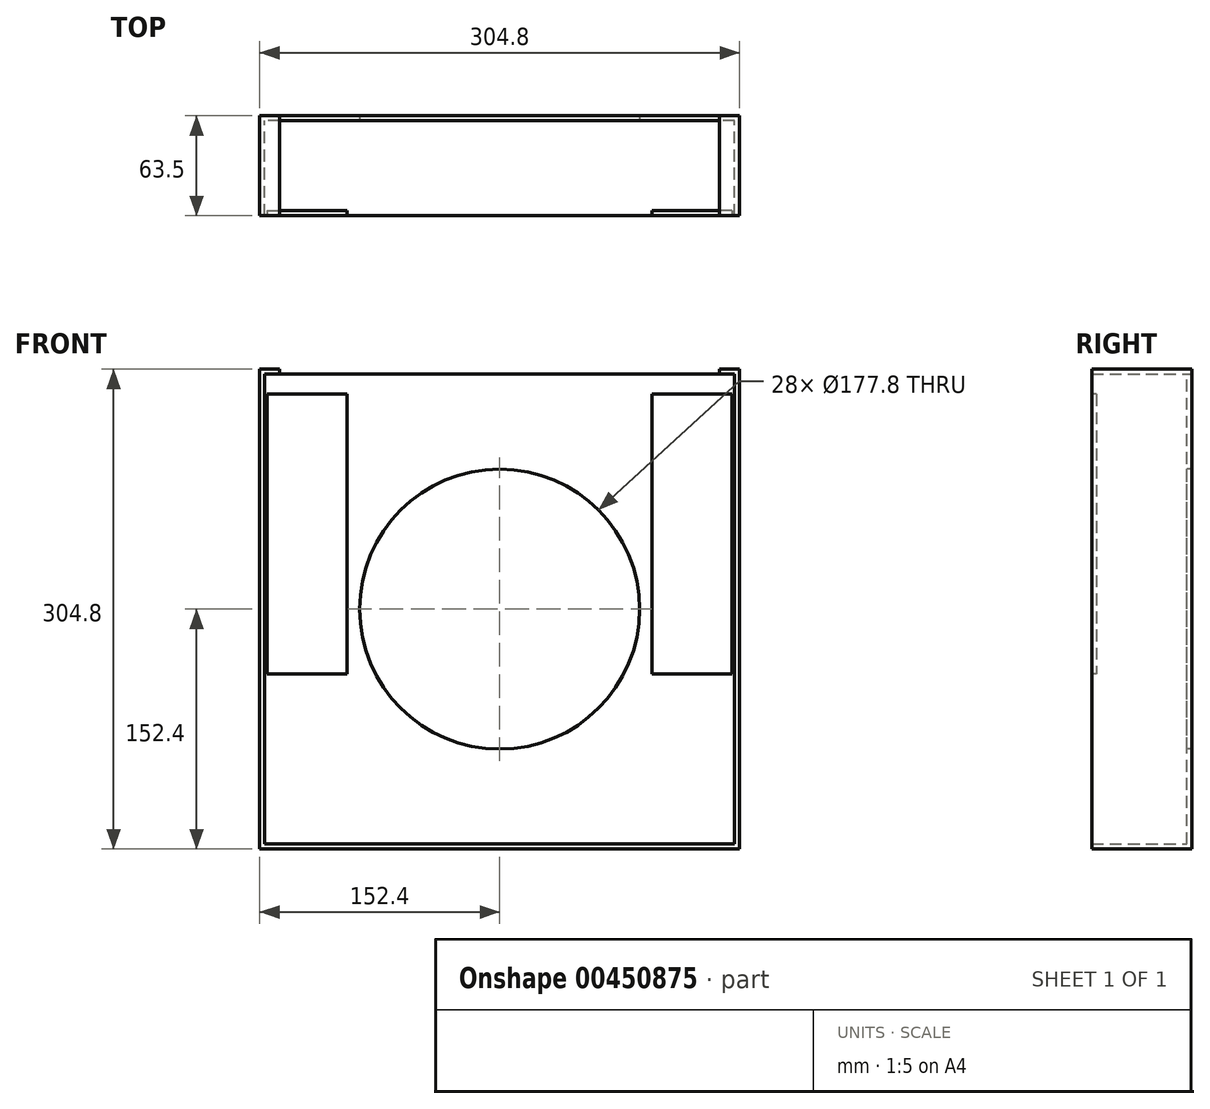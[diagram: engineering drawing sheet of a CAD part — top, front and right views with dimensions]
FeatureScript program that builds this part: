
annotation { "Feature Type Name" : "Feature", "Feature Type Description" : "" }
export const myFeature = defineFeature(function(context is Context, id is Id, definition is map)
    precondition{}
    {
        {
            var Q0;
            Q0=qCreatedBy(makeId("Front.planeOp"),FACE);
            var sketch = newSketch(context, id + "F0", { "sketchPlane" : qUnion([Q0])});
            skLineSegment(sketch, "E0.bottom", {"start": v(152.4, -152.4) * mm, "end": v(-152.4, -152.4) * mm});
            skLineSegment(sketch, "E0.top", {"start": v(152.4, 152.4) * mm, "end": v(-152.4, 152.4) * mm});
            skLineSegment(sketch, "E0.left", {"start": v(152.4, -152.4) * mm, "end": v(152.4, 152.4) * mm});
            skLineSegment(sketch, "E0.right", {"start": v(-152.4, -152.4) * mm, "end": v(-152.4, 152.4) * mm});
            skPoint(sketch, "E0.middle", {"position": v(0, 0) * mm});
            skSolve(sketch);
        }
        {
            var Q0;
            Q0=qSketchRegion(id+"F0",true);
            extrude(context, id + "F1", {"entities" : qUnion([Q0]), "depth" : 63.5 * mm});
        }
        {
            var Q0;
            Q0=makeQuery(id+"F1.opExtrude","CAP_FACE",FACE,{"disambiguationData":[OSD([sQuery(id+"F0.wireOp",EDGE,"E0.bottom"),sQuery(id+"F0.wireOp",EDGE,"E0.top"),sQuery(id+"F0.wireOp",EDGE,"E0.left"),sQuery(id+"F0.wireOp",EDGE,"E0.right")])],"isStart":false});
            shell(context, id + "F2", {"entities" : qUnion([Q0]), "thickness" : 3.17 * mm});
        }
        {
            var Q0;
            Q0=makeQuery(id+"F2.opShell","OFFSET_FACE",FACE,{"disambiguationData":[OSD([sQuery(id+"F0.wireOp",EDGE,"E0.bottom"),sQuery(id+"F0.wireOp",EDGE,"E0.top"),sQuery(id+"F0.wireOp",EDGE,"E0.left"),sQuery(id+"F0.wireOp",EDGE,"E0.right")])]});
            var sketch = newSketch(context, id + "F3", { "sketchPlane" : qUnion([Q0])});
            skCircle(sketch, "E1", {"center": v(0, 0) * mm, "radius": 88.9 * mm});
            skSolve(sketch);
        }
        {
            var Q0;
            Q0=qSketchRegion(id+"F3",true);
            extrude(context, id + "F4", {"entities" : qUnion([Q0]), "operationType" : NewBodyOperationType.REMOVE, "endBound" : BoundingType.UP_TO_NEXT, "oppositeDirection" : true, "depth" : 25.4 * mm});
        }
        {
            var Q0;
            Q0=makeQuery(id+"F1.opExtrude","CAP_FACE",FACE,{"disambiguationData":[OSD([sQuery(id+"F0.wireOp",EDGE,"E0.bottom"),sQuery(id+"F0.wireOp",EDGE,"E0.top"),sQuery(id+"F0.wireOp",EDGE,"E0.left"),sQuery(id+"F0.wireOp",EDGE,"E0.right")])],"isStart":false});
            var sketch = newSketch(context, id + "F5", { "sketchPlane" : qUnion([Q0])});
            skLineSegment(sketch, "E2.bottom", {"start": v(-147.64, 136.53) * mm, "end": v(-96.84, 136.53) * mm});
            skLineSegment(sketch, "E2.top", {"start": v(-147.64, -41.28) * mm, "end": v(-96.84, -41.28) * mm});
            skLineSegment(sketch, "E2.left", {"start": v(-147.64, 136.53) * mm, "end": v(-147.64, -41.28) * mm});
            skLineSegment(sketch, "E2.right", {"start": v(-96.84, 136.53) * mm, "end": v(-96.84, -41.28) * mm});
            skLineSegment(sketch, "E3.MirrorCS", {"start": v(147.64, 136.53) * mm, "end": v(96.84, 136.53) * mm});
            skLineSegment(sketch, "E4.MirrorCS", {"start": v(96.84, 136.53) * mm, "end": v(96.84, -41.28) * mm});
            skLineSegment(sketch, "E5.MirrorCS", {"start": v(147.64, -41.27) * mm, "end": v(96.84, -41.27) * mm});
            skLineSegment(sketch, "E6.MirrorCS", {"start": v(147.64, 136.53) * mm, "end": v(147.64, -41.28) * mm});
            skSolve(sketch);
        }
        {
            var Q0;
            Q0=makeQuery(id+"F5.imprint","IMPRINT",FACE,{"disambiguationData":[TD([[makeQuery(id+"F5.imprint","IMPRINT",EDGE,{"derivedFrom":sQuery(id+"F5.wireOp",EDGE,"E2.bottom")}),-1.0]])]});
            var Q1;
            Q1=makeQuery(id+"F5.imprint","IMPRINT",FACE,{"disambiguationData":[TD([[makeQuery(id+"F5.imprint","IMPRINT",EDGE,{"derivedFrom":sQuery(id+"F5.wireOp",EDGE,"E3.MirrorCS")}),1.0]])]});
            extrude(context, id + "F6", {"entities" : qUnion([Q0, Q1]), "oppositeDirection" : true, "depth" : 3.17 * mm});
        }
        {
            var Q0;
            Q0=makeQuery(id+"F1.opExtrude","SWEPT_FACE",FACE,{"disambiguationData":[OSD([sQuery(id+"F0.wireOp",EDGE,"E0.top")])]});
            var sketch = newSketch(context, id + "F7", { "sketchPlane" : qUnion([Q0])});
            skLineSegment(sketch, "E7.bottom", {"start": v(-139.7, -63.5) * mm, "end": v(139.7, -63.5) * mm});
            skLineSegment(sketch, "E7.top", {"start": v(-139.7, 0) * mm, "end": v(139.7, 0) * mm});
            skLineSegment(sketch, "E7.left", {"start": v(-139.7, -63.5) * mm, "end": v(-139.7, 0) * mm});
            skLineSegment(sketch, "E7.right", {"start": v(139.7, -63.5) * mm, "end": v(139.7, 0) * mm});
            skSolve(sketch);
        }
        {
            var Q0;
            Q0=qSketchRegion(id+"F7",true);
            extrude(context, id + "F8", {"entities" : qUnion([Q0]), "operationType" : NewBodyOperationType.REMOVE, "oppositeDirection" : true, "depth" : 3.17 * mm});
        }
        {
            var Q0;
            Q0=makeQuery(id+"F1.opExtrude","SWEPT_BODY",BODY,{"disambiguationData":[OSD([sQuery(id+"F0.wireOp",EDGE,"E0.bottom"),sQuery(id+"F0.wireOp",EDGE,"E0.top"),sQuery(id+"F0.wireOp",EDGE,"E0.left"),sQuery(id+"F0.wireOp",EDGE,"E0.right")])]});
            transform(context, id + "F9", {"entities" : qUnion([Q0]), "transformType" : TransformType.TRANSLATION_3D, "dx" : 0 * mm, "dy" : 0 * mm, "dz" : 0 * mm, "makeCopy" : true});
        }
    });
